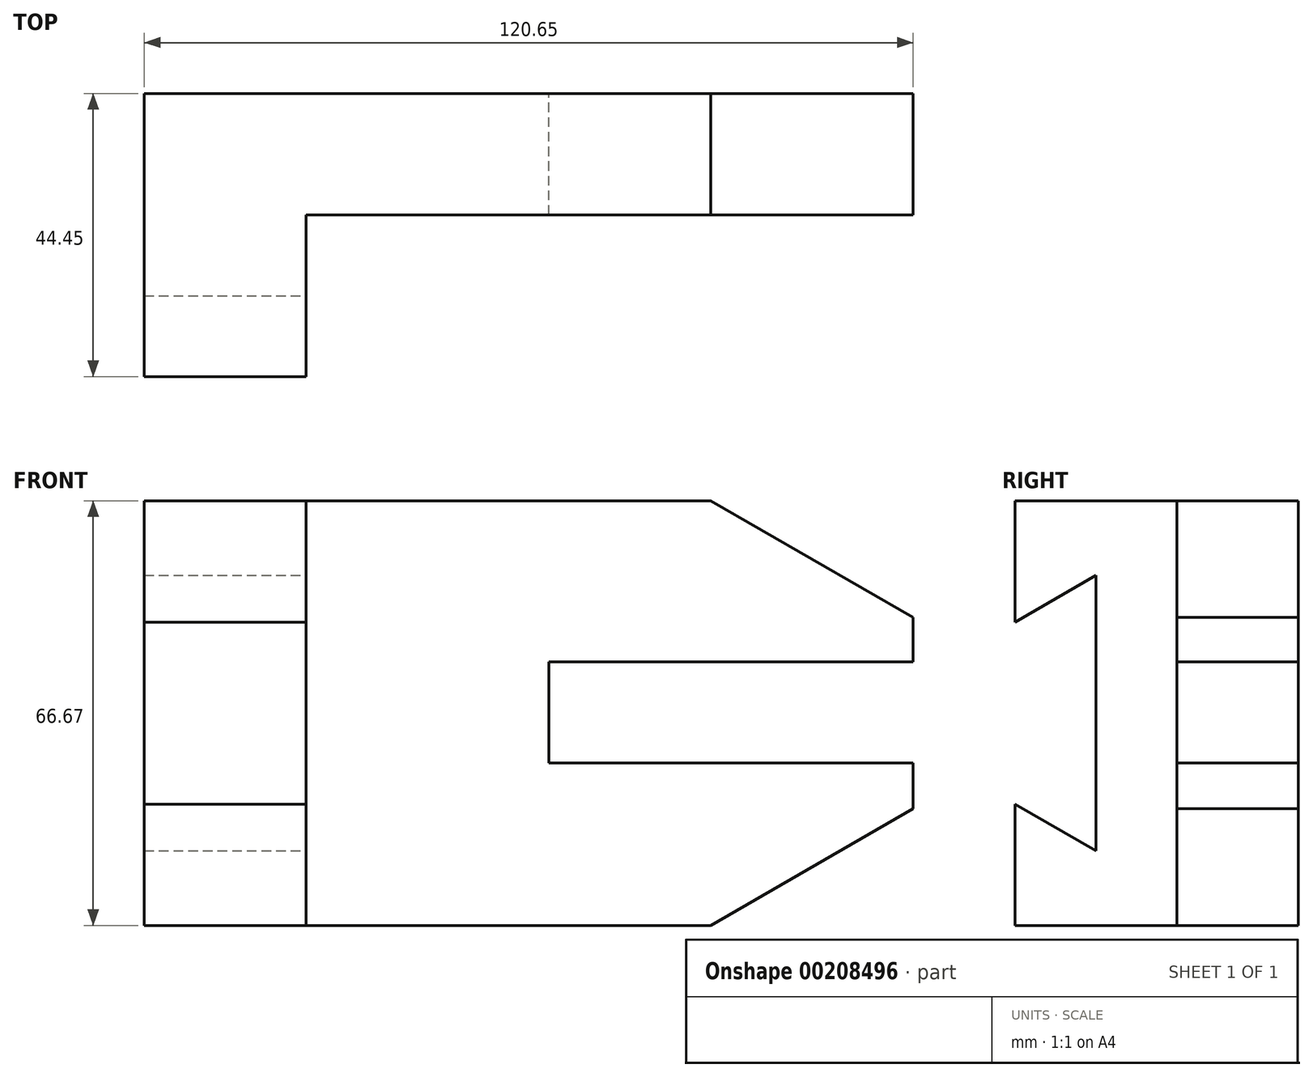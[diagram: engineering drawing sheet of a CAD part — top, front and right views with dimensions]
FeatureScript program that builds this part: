
annotation { "Feature Type Name" : "Feature", "Feature Type Description" : "" }
export const myFeature = defineFeature(function(context is Context, id is Id, definition is map)
    precondition{}
    {
        {
            var Q0;
            Q0=qCreatedBy(makeId("Front.planeOp"),FACE);
            var sketch = newSketch(context, id + "F0", { "sketchPlane" : qUnion([Q0])});
            skLineSegment(sketch, "E0.bottom", {"start": v(-53.7, 30.56) * mm, "end": v(35.2, 30.56) * mm});
            skLineSegment(sketch, "E0.top", {"start": v(-53.7, -36.11) * mm, "end": v(35.2, -36.11) * mm});
            skLineSegment(sketch, "E0.left", {"start": v(-53.7, 30.56) * mm, "end": v(-53.7, -36.11) * mm});
            skLineSegment(sketch, "E0.right", {"start": v(66.95, 12.23) * mm, "end": v(66.95, 5.25) * mm});
            skLineSegment(sketch, "E1", {"start": v(35.2, -36.11) * mm, "end": v(66.95, -17.78) * mm});
            skLineSegment(sketch, "E2.MirrorCS", {"start": v(35.2, 30.56) * mm, "end": v(66.95, 12.23) * mm});
            skPoint(sketch, "E3.orphan", {"position": v(66.95, 30.56) * mm});
            skPoint(sketch, "E4.orphan", {"position": v(66.95, -36.11) * mm});
            skLineSegment(sketch, "E5.bottom", {"start": v(66.95, 5.25) * mm, "end": v(9.8, 5.25) * mm});
            skLineSegment(sketch, "E5.top", {"start": v(66.95, -10.62) * mm, "end": v(9.8, -10.62) * mm});
            skLineSegment(sketch, "E5.right", {"start": v(9.8, 5.25) * mm, "end": v(9.8, -10.62) * mm});
            skLineSegment(sketch, "E6.trimOffspring", {"start": v(66.95, -10.62) * mm, "end": v(66.95, -17.78) * mm});
            skPoint(sketch, "E7.start.orphan", {"position": v(66.95, -2.78) * mm});
            skSolve(sketch);
        }
        {
            var Q0;
            Q0 = qSketchRegion(id + "F0", true);
            extrude(context, id + "F1", {"entities" : qUnion([Q0]), "depth" : 19.05 * mm});
        }
        {
            var Q0;
            Q0=makeQuery(id+"F1.opExtrude","CAP_FACE",FACE,{"disambiguationData":[OSD([sQuery(id+"F0.wireOp",EDGE,"E0.bottom"),sQuery(id+"F0.wireOp",EDGE,"E0.top"),sQuery(id+"F0.wireOp",EDGE,"E0.left"),sQuery(id+"F0.wireOp",EDGE,"E0.right"),sQuery(id+"F0.wireOp",EDGE,"E1"),sQuery(id+"F0.wireOp",EDGE,"E2.MirrorCS"),sQuery(id+"F0.wireOp",EDGE,"E5.bottom"),sQuery(id+"F0.wireOp",EDGE,"E5.top"),sQuery(id+"F0.wireOp",EDGE,"E5.right"),sQuery(id+"F0.wireOp",EDGE,"E6.trimOffspring")])],"isStart":false});
            var sketch = newSketch(context, id + "F2", { "sketchPlane" : qUnion([Q0])});
            skLineSegment(sketch, "E8.bottom", {"start": v(-53.7, 30.56) * mm, "end": v(-28.3, 30.56) * mm});
            skLineSegment(sketch, "E8.top", {"start": v(-53.7, -36.11) * mm, "end": v(-28.3, -36.11) * mm});
            skLineSegment(sketch, "E8.left", {"start": v(-53.7, 30.56) * mm, "end": v(-53.7, -36.11) * mm});
            skLineSegment(sketch, "E8.right", {"start": v(-28.3, 30.56) * mm, "end": v(-28.3, -36.11) * mm});
            skSolve(sketch);
        }
        {
            var Q0;
            Q0 = qSketchRegion(id + "F2", true);
            extrude(context, id + "F3", {"entities" : qUnion([Q0]), "operationType" : NewBodyOperationType.ADD, "depth" : 25.4 * mm});
        }
        {
            var Q0;
            Q0=makeQuery(id+"F3.opExtrude","SWEPT_FACE",FACE,{"disambiguationData":[OSD([sQuery(id+"F2.wireOp",EDGE,"E8.right")])]});
            var sketch = newSketch(context, id + "F4", { "sketchPlane" : qUnion([Q0])});
            skLineSegment(sketch, "E9", {"start": v(-44.45, 11.51) * mm, "end": v(-31.75, 18.84) * mm});
            skLineSegment(sketch, "E10", {"start": v(-44.45, -17.06) * mm, "end": v(-31.75, -24.4) * mm});
            skLineSegment(sketch, "E11", {"start": v(-31.75, -24.4) * mm, "end": v(-31.75, 18.84) * mm});
            skSolve(sketch);
        }
        {
            var Q0;
            Q0 = qSketchRegion(id + "F4", true);
            var Q1;
            {var subQ0=sQuery(id+"F4.wireOp",EDGE,"E9");Q1=makeQuery(id+"F4.imprint","IMPRINT",FACE,{"disambiguationData":[TD([[makeQuery(id+"F4.imprint","IMPRINT",EDGE,{"derivedFrom":subQ0}),-1.0]])]});}
            extrude(context, id + "F5", {"entities" : qUnion([Q0, Q1]), "operationType" : NewBodyOperationType.REMOVE, "endBound" : BoundingType.THROUGH_ALL, "oppositeDirection" : true, "depth" : 25.4 * mm});
        }
    });
